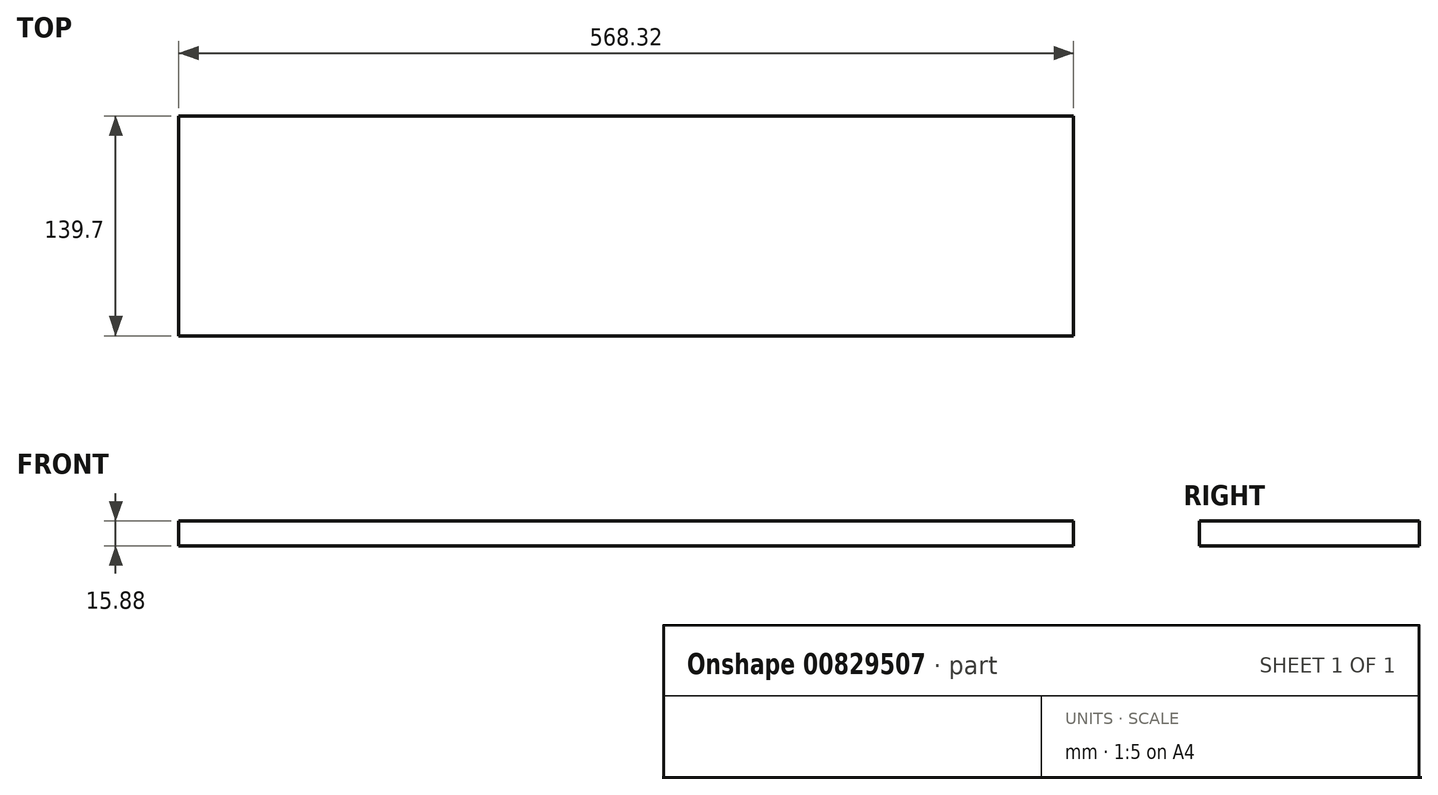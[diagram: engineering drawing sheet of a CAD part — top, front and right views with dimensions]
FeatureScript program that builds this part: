
annotation { "Feature Type Name" : "Feature", "Feature Type Description" : "" }
export const myFeature = defineFeature(function(context is Context, id is Id, definition is map)
    precondition{}
    {
        {
            var Q0;
            Q0=qCreatedBy(makeId("Right.planeOp"),FACE);
            var sketch = newSketch(context, id + "F0", { "sketchPlane" : qUnion([Q0])});
            skLineSegment(sketch, "E0.bottom", {"start": v(0, 0) * mm, "end": v(139.7, 0) * mm});
            skLineSegment(sketch, "E0.top", {"start": v(0, -15.87) * mm, "end": v(139.7, -15.87) * mm});
            skLineSegment(sketch, "E0.left", {"start": v(0, 0) * mm, "end": v(0, -15.87) * mm});
            skLineSegment(sketch, "E0.right", {"start": v(139.7, 0) * mm, "end": v(139.7, -15.87) * mm});
            skSolve(sketch);
        }
        {
            var Q0;
            Q0=makeQuery(id+"F0.imprint","IMPRINT",FACE,{"disambiguationData":[TD([[makeQuery(id+"F0.imprint","IMPRINT",EDGE,{"derivedFrom":sQuery(id+"F0.wireOp",EDGE,"E0.bottom")}),-1.0]])]});
            extrude(context, id + "F1", {"entities" : qUnion([Q0]), "depth" : 568.32 * mm, "offsetDistance" : 25.4 * mm});
        }
    });
